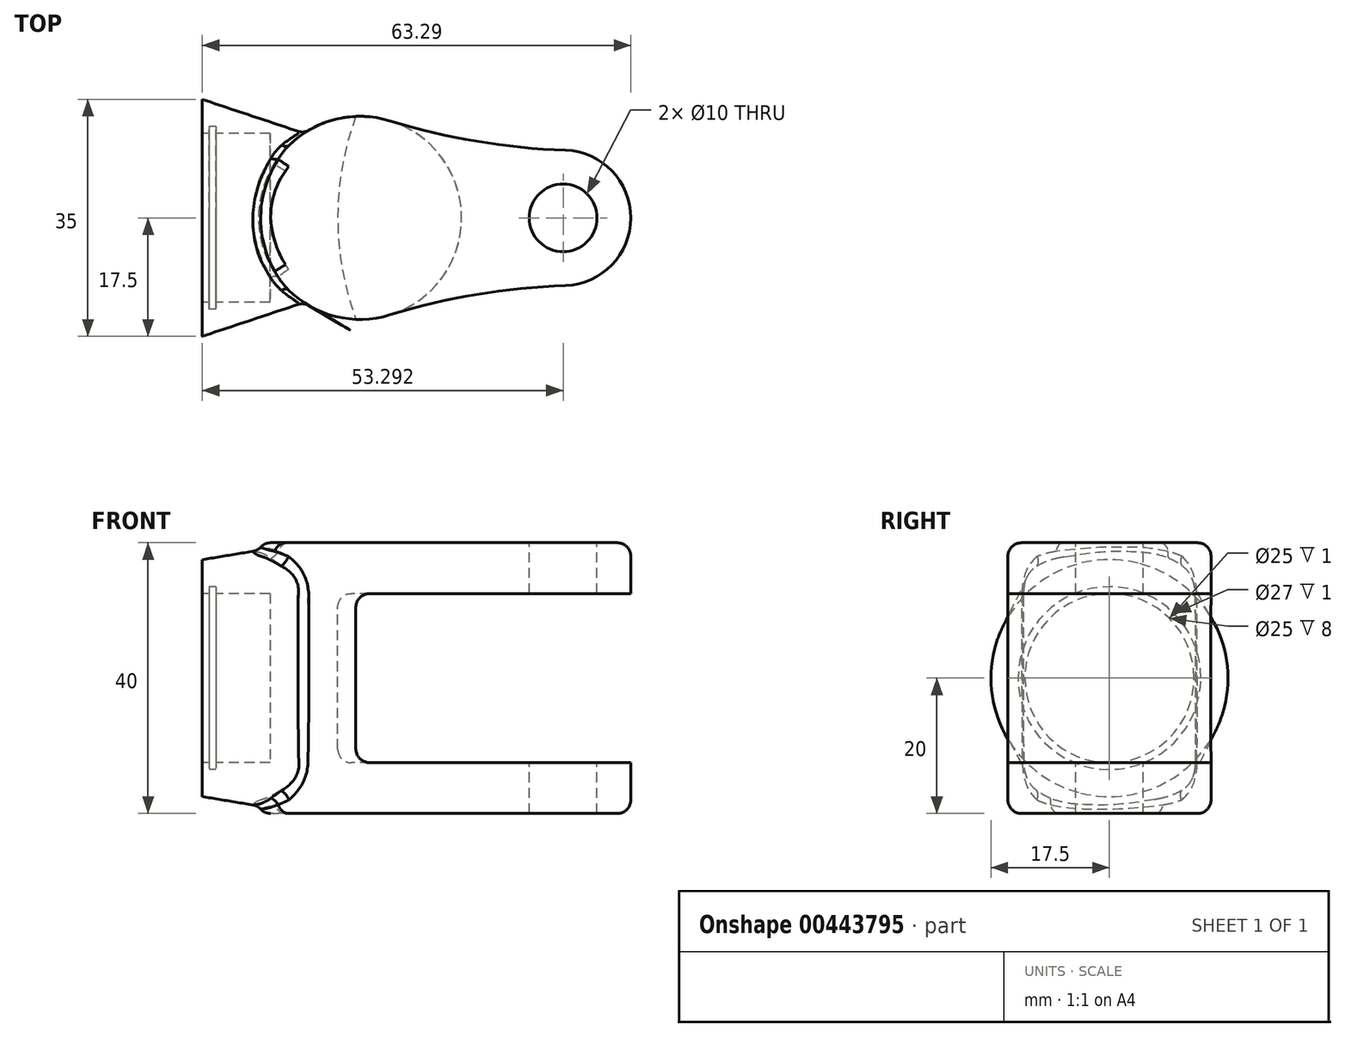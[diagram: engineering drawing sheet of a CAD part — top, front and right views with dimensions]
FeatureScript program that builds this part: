
annotation { "Feature Type Name" : "Feature", "Feature Type Description" : "" }
export const myFeature = defineFeature(function(context is Context, id is Id, definition is map)
    precondition{}
    {
        {
            var Q0;
            Q0=qCreatedBy(makeId("Right.planeOp"),FACE);
            var sketch = newSketch(context, id + "F0", { "sketchPlane" : qUnion([Q0])});
            skCircle(sketch, "E0", {"center": v(0, 0) * mm, "radius": 17.5 * mm});
            skSolve(sketch);
        }
        {
            var Q0;
            Q0=qCreatedBy(makeId("Right.planeOp"),FACE);
            cPlane(context, id + "F1", {"entities" : qUnion([Q0]), "cplaneType" : CPlaneType.OFFSET, "offset" : 15 * mm, "width" : 150 * mm, "height" : 150 * mm});
        }
        {
            var Q0;
            Q0=qCreatedBy(id+"F1.planeOp",FACE);
            var sketch = newSketch(context, id + "F2", { "sketchPlane" : qUnion([Q0])});
            skLineSegment(sketch, "E1.bottom", {"start": v(5, 20) * mm, "end": v(-5, 20) * mm});
            skLineSegment(sketch, "E1.top", {"start": v(5, -20) * mm, "end": v(-5, -20) * mm});
            skLineSegment(sketch, "E1.left", {"start": v(12.5, 12.5) * mm, "end": v(12.5, -12.5) * mm});
            skLineSegment(sketch, "E1.right", {"start": v(-12.5, 12.5) * mm, "end": v(-12.5, -12.5) * mm});
            skPoint(sketch, "E1.middle", {"position": v(0, 0) * mm});
            skPoint(sketch, "E2.visualSharp", {"position": v(-12.5, 20) * mm});
            skArc(sketch, "E2.filletArc", {"start": v(-5, 20) * mm, "mid": v(-10.3, 17.8) * mm, "end": v(-12.5, 12.5) * mm});
            skPoint(sketch, "E3.visualSharp", {"position": v(12.5, 20) * mm});
            skArc(sketch, "E3.filletArc", {"start": v(12.5, 12.5) * mm, "mid": v(10.3, 17.8) * mm, "end": v(5, 20) * mm});
            skPoint(sketch, "E4.visualSharp", {"position": v(12.5, -20) * mm});
            skArc(sketch, "E4.filletArc", {"start": v(5, -20) * mm, "mid": v(10.3, -17.8) * mm, "end": v(12.5, -12.5) * mm});
            skPoint(sketch, "E5.visualSharp", {"position": v(-12.5, -20) * mm});
            skArc(sketch, "E5.filletArc", {"start": v(-12.5, -12.5) * mm, "mid": v(-10.3, -17.8) * mm, "end": v(-5, -20) * mm});
            skSolve(sketch);
        }
        {
            var Q0;
            Q0=makeQuery(id+"F2.imprint","IMPRINT",FACE,{"disambiguationData":[TD([[makeQuery(id+"F2.imprint","IMPRINT",EDGE,{"derivedFrom":sQuery(id+"F2.wireOp",EDGE,"E1.bottom")}),1.0]])]});
            var Q1;
            Q1=makeQuery(id+"F0.imprint","IMPRINT",FACE,{"disambiguationData":[TD([[makeQuery(id+"F0.imprint","IMPRINT",EDGE,{"derivedFrom":sQuery(id+"F0.wireOp",EDGE,"E0")}),1.0]])]});
            loft(context, id + "F3", {"sheetProfilesArray" : [{ "sheetProfileEntities" : qUnion([Q0]) }, { "sheetProfileEntities" : qUnion([Q1]) }]});
        }
        {
            var Q0;
            Q0=qCreatedBy(makeId("Top.planeOp"),FACE);
            var sketch = newSketch(context, id + "F4", { "sketchPlane" : qUnion([Q0])});
            skArc(sketch, "E6", {"start": v(27.7, 14.34) * mm, "mid": v(8.3, 0) * mm, "end": v(27.7, -14.34) * mm});
            skArc(sketch, "E7", {"start": v(53.63, -10) * mm, "mid": v(63.3, 0) * mm, "end": v(53.63, 10) * mm});
            skArc(sketch, "E8", {"start": v(27.7, 14.34) * mm, "mid": v(40.52, 11.31) * mm, "end": v(53.63, 10) * mm});
            skArc(sketch, "E9", {"start": v(53.63, -10) * mm, "mid": v(40.52, -11.31) * mm, "end": v(27.7, -14.34) * mm});
            skSolve(sketch);
        }
        {
            var Q0;
            Q0 = qSketchRegion(id + "F4", true);
            extrude(context, id + "F5", {"entities" : qUnion([Q0]), "operationType" : NewBodyOperationType.ADD, "endBound" : BoundingType.SYMMETRIC, "depth" : 40 * mm});
        }
        {
            var Q0;
            Q0=qCreatedBy(makeId("Front.planeOp"),FACE);
            var sketch = newSketch(context, id + "F6", { "sketchPlane" : qUnion([Q0])});
            skLineSegment(sketch, "E10.bottom", {"start": v(63.3, -12.5) * mm, "end": v(20, -12.5) * mm});
            skLineSegment(sketch, "E10.top", {"start": v(63.3, 12.5) * mm, "end": v(20, 12.5) * mm});
            skLineSegment(sketch, "E10.left", {"start": v(63.3, -12.5) * mm, "end": v(63.3, 12.5) * mm});
            skLineSegment(sketch, "E10.right", {"start": v(20, -12.5) * mm, "end": v(20, 12.5) * mm});
            skPoint(sketch, "E10.middle", {"position": v(41.65, 0) * mm});
            skSolve(sketch);
        }
        {
            var Q0;
            Q0 = qSketchRegion(id + "F6", true);
            var Q1;
            Q1=sQuery(id+"F6.wireOp",EDGE,"E10.left");
            revolve(context, id + "F7", {"operationType" : NewBodyOperationType.REMOVE, "entities" : qUnion([Q0]), "axis" : qUnion([Q1]), "revolveType" : RevolveType.FULL, "oppositeDirection" : true});
        }
        {
            var Q0;
            Q0=makeQuery(id+"F3.opLoft","CAP_FACE",FACE,{"disambiguationData":[OSD([makeQuery(id+"F0.imprint","IMPRINT",FACE,{"disambiguationData":[TD([[makeQuery(id+"F0.imprint","IMPRINT",EDGE,{"derivedFrom":sQuery(id+"F0.wireOp",EDGE,"E0")}),1.0]])]})])],"isStart":true});
            var sketch = newSketch(context, id + "F8", { "sketchPlane" : qUnion([Q0])});
            skCircle(sketch, "E11", {"center": v(0, 0) * mm, "radius": 12.5 * mm});
            skSolve(sketch);
        }
        {
            var Q0;
            Q0=makeQuery(id+"F8.imprint","IMPRINT",FACE,{"disambiguationData":[TD([[makeQuery(id+"F8.imprint","IMPRINT",EDGE,{"derivedFrom":sQuery(id+"F8.wireOp",EDGE,"E11")}),1.0]])]});
            extrude(context, id + "F9", {"entities" : qUnion([Q0]), "operationType" : NewBodyOperationType.REMOVE, "oppositeDirection" : true, "depth" : 10 * mm});
        }
        {
            var Q0;
            Q0=makeQuery(id+"F3.opLoft","CAP_FACE",FACE,{"disambiguationData":[OSD([makeQuery(id+"F0.imprint","IMPRINT",FACE,{"disambiguationData":[TD([[makeQuery(id+"F0.imprint","IMPRINT",EDGE,{"derivedFrom":sQuery(id+"F0.wireOp",EDGE,"E0")}),1.0]])]})])],"isStart":true});
            cPlane(context, id + "F10", {"entities" : qUnion([Q0]), "cplaneType" : CPlaneType.OFFSET, "offset" : 1 * mm, "oppositeDirection" : true, "width" : 150 * mm, "height" : 150 * mm});
        }
        {
            var Q0;
            Q0=qCreatedBy(id+"F10.planeOp",FACE);
            var sketch = newSketch(context, id + "F11", { "sketchPlane" : qUnion([Q0])});
            skCircle(sketch, "E12.0", {"center": v(0, 0) * mm, "radius": 13.5 * mm});
            skSolve(sketch);
        }
        {
            var Q0;
            Q0 = qSketchRegion(id + "F11", true);
            extrude(context, id + "F12", {"entities" : qUnion([Q0]), "operationType" : NewBodyOperationType.REMOVE, "oppositeDirection" : true, "depth" : 1 * mm});
        }
        {
            var Q0;
            Q0=makeQuery(id+"F5.opExtrude","CAP_FACE",FACE,{"disambiguationData":[OSD([sQuery(id+"F4.wireOp",EDGE,"E6"),sQuery(id+"F4.wireOp",EDGE,"E7"),sQuery(id+"F4.wireOp",EDGE,"E8"),sQuery(id+"F4.wireOp",EDGE,"E9")])],"isStart":false});
            var sketch = newSketch(context, id + "F13", { "sketchPlane" : qUnion([Q0])});
            skCircle(sketch, "E13", {"center": v(53.3, 0) * mm, "radius": 5 * mm});
            skSolve(sketch);
        }
        {
            var Q0;
            Q0 = qSketchRegion(id + "F13", true);
            extrude(context, id + "F14", {"entities" : qUnion([Q0]), "operationType" : NewBodyOperationType.REMOVE, "endBound" : BoundingType.THROUGH_ALL, "oppositeDirection" : true, "depth" : 25 * mm});
        }
        {
            var Q0;
            Q0=makeQuery(id+"F7.boolean.opBoolean","COPY",EDGE,{"derivedFrom":makeQuery(id+"F7.opRevolve","SWEPT_EDGE",EDGE,{"disambiguationData":[OSD([sQuery(id+"F6.wireOp",EDGE,"E10.bottom"),sQuery(id+"F6.wireOp",EDGE,"E10.right")])]})});
            var Q1;
            Q1=makeQuery(id+"F7.boolean.opBoolean","COPY",EDGE,{"derivedFrom":makeQuery(id+"F7.opRevolve","SWEPT_EDGE",EDGE,{"disambiguationData":[OSD([sQuery(id+"F6.wireOp",EDGE,"E10.top"),sQuery(id+"F6.wireOp",EDGE,"E10.right")])]})});
            var Q2;
            Q2=makeQuery(id+"F5.opExtrude","CAP_EDGE",EDGE,{"disambiguationData":[OSD([sQuery(id+"F4.wireOp",EDGE,"E8")])],"isStart":true});
            var Q3;
            Q3=makeQuery(id+"F5.opExtrude","CAP_EDGE",EDGE,{"disambiguationData":[OSD([sQuery(id+"F4.wireOp",EDGE,"E7")])],"isStart":true});
            var Q4;
            Q4=makeQuery(id+"F5.opExtrude","CAP_EDGE",EDGE,{"disambiguationData":[OSD([sQuery(id+"F4.wireOp",EDGE,"E9")])],"isStart":true});
            var Q5;
            Q5=makeQuery(id+"F5.opExtrude","CAP_EDGE",EDGE,{"disambiguationData":[OSD([sQuery(id+"F4.wireOp",EDGE,"E6")])],"isStart":true});
            var Q6;
            Q6=makeQuery(id+"F5.opExtrude","CAP_EDGE",EDGE,{"disambiguationData":[OSD([sQuery(id+"F4.wireOp",EDGE,"E9")])],"isStart":false});
            var Q7;
            Q7=makeQuery(id+"F5.opExtrude","CAP_EDGE",EDGE,{"disambiguationData":[OSD([sQuery(id+"F4.wireOp",EDGE,"E6")])],"isStart":false});
            var Q8;
            Q8=makeQuery(id+"F5.opExtrude","CAP_EDGE",EDGE,{"disambiguationData":[OSD([sQuery(id+"F4.wireOp",EDGE,"E7")])],"isStart":false});
            var Q9;
            Q9=makeQuery(id+"F5.opExtrude","CAP_EDGE",EDGE,{"disambiguationData":[OSD([sQuery(id+"F4.wireOp",EDGE,"E8")])],"isStart":false});
            fillet(context, id + "F15", {"entities" : qUnion([Q0, Q1, Q2, Q3, Q4, Q5, Q6, Q7, Q8, Q9]), "radius" : 2 * mm, "tangentPropagation" : true, "allowEdgeOverflow" : false});
        }
        {
            var Q0;
            Q0=makeQuery(id+"F15.opFillet","BLEND_EDGE",EDGE,{"blendedFrom":[makeQuery(id+"F5.opExtrude","CAP_EDGE",EDGE,{"disambiguationData":[OSD([sQuery(id+"F4.wireOp",EDGE,"E6")])],"isStart":true}),makeQuery(id+"F3.opLoft","SWEPT_FACE",FACE,{"disambiguationData":[OSD([sQuery(id+"F0.wireOp",EDGE,"E0"),sQuery(id+"F2.wireOp",EDGE,"E1.bottom"),sQuery(id+"F2.wireOp",EDGE,"E1.left"),sQuery(id+"F2.wireOp",EDGE,"E3.filletArc")])]})],"blendedInto":[makeQuery(id+"F3.opLoft","SWEPT_FACE",FACE,{"disambiguationData":[OSD([sQuery(id+"F0.wireOp",EDGE,"E0"),sQuery(id+"F2.wireOp",EDGE,"E1.bottom"),sQuery(id+"F2.wireOp",EDGE,"E1.left"),sQuery(id+"F2.wireOp",EDGE,"E3.filletArc")])]})]});
            var Q1;
            Q1=makeQuery(id+"F5.boolean.opBoolean","INTERSECT",EDGE,{"disambiguationData":[OD(1.0)],"derivedFrom":[makeQuery(id+"F3.opLoft","SWEPT_FACE",FACE,{"disambiguationData":[OSD([sQuery(id+"F0.wireOp",EDGE,"E0"),sQuery(id+"F2.wireOp",EDGE,"E1.bottom"),sQuery(id+"F2.wireOp",EDGE,"E1.left"),sQuery(id+"F2.wireOp",EDGE,"E3.filletArc")])]}),makeQuery(id+"F5.opExtrude","SWEPT_FACE",FACE,{"disambiguationData":[OSD([sQuery(id+"F4.wireOp",EDGE,"E6")])]})]});
            var Q2;
            Q2=makeQuery(id+"F3.opLoft","MID_CAP_EDGE",EDGE,{"disambiguationData":[OSD([sQuery(id+"F2.wireOp",EDGE,"E1.left"),sQuery(id+"F2.wireOp",EDGE,"E3.filletArc"),sQuery(id+"F2.wireOp",EDGE,"E4.filletArc")])],"capPos":0.0});
            var Q3;
            Q3=makeQuery(id+"F5.boolean.opBoolean","INTERSECT",EDGE,{"disambiguationData":[OD(0.0)],"derivedFrom":[makeQuery(id+"F3.opLoft","SWEPT_FACE",FACE,{"disambiguationData":[OSD([sQuery(id+"F0.wireOp",EDGE,"E0"),sQuery(id+"F2.wireOp",EDGE,"E1.bottom"),sQuery(id+"F2.wireOp",EDGE,"E1.left"),sQuery(id+"F2.wireOp",EDGE,"E3.filletArc")])]}),makeQuery(id+"F5.opExtrude","SWEPT_FACE",FACE,{"disambiguationData":[OSD([sQuery(id+"F4.wireOp",EDGE,"E6")])]})]});
            var Q4;
            Q4=makeQuery(id+"F15.opFillet","BLEND_EDGE",EDGE,{"blendedFrom":[makeQuery(id+"F5.opExtrude","CAP_EDGE",EDGE,{"disambiguationData":[OSD([sQuery(id+"F4.wireOp",EDGE,"E6")])],"isStart":false}),makeQuery(id+"F3.opLoft","SWEPT_FACE",FACE,{"disambiguationData":[OSD([sQuery(id+"F0.wireOp",EDGE,"E0"),sQuery(id+"F2.wireOp",EDGE,"E1.bottom"),sQuery(id+"F2.wireOp",EDGE,"E1.left"),sQuery(id+"F2.wireOp",EDGE,"E3.filletArc")])]})],"blendedInto":[makeQuery(id+"F3.opLoft","SWEPT_FACE",FACE,{"disambiguationData":[OSD([sQuery(id+"F0.wireOp",EDGE,"E0"),sQuery(id+"F2.wireOp",EDGE,"E1.bottom"),sQuery(id+"F2.wireOp",EDGE,"E1.left"),sQuery(id+"F2.wireOp",EDGE,"E3.filletArc")])]})]});
            var Q5;
            Q5=makeQuery(id+"F3.opLoft","MID_CAP_EDGE",EDGE,{"disambiguationData":[OSD([sQuery(id+"F2.wireOp",EDGE,"E1.right"),sQuery(id+"F2.wireOp",EDGE,"E2.filletArc"),sQuery(id+"F2.wireOp",EDGE,"E5.filletArc")])],"capPos":0.0});
            fillet(context, id + "F16", {"entities" : qUnion([Q0, Q1, Q2, Q3, Q4, Q5]), "radius" : 2 * mm, "tangentPropagation" : true, "allowEdgeOverflow" : false});
        }
    });
